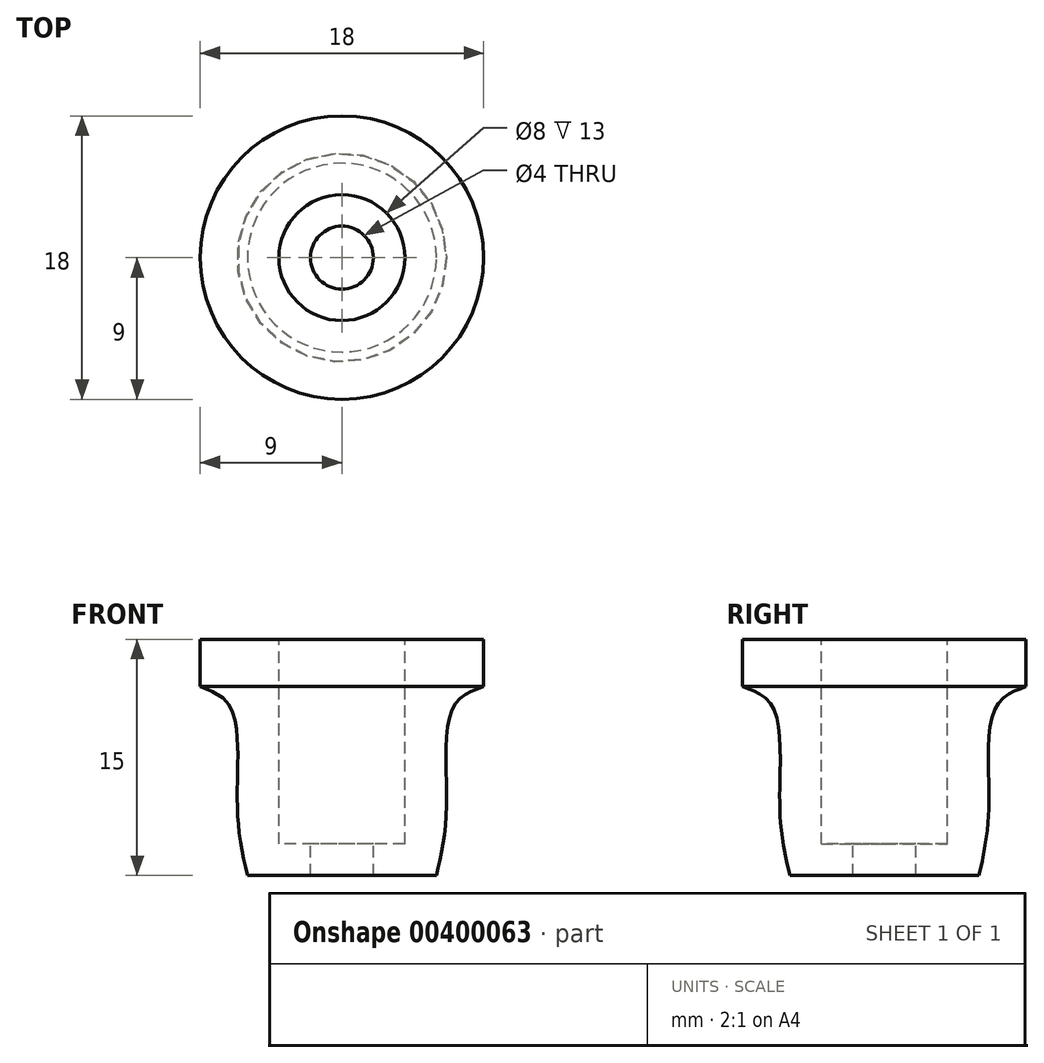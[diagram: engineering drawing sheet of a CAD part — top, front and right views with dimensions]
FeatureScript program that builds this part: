
annotation { "Feature Type Name" : "Feature", "Feature Type Description" : "" }
export const myFeature = defineFeature(function(context is Context, id is Id, definition is map)
    precondition{}
    {
        {
            var Q0;
            Q0=qCreatedBy(makeId("Front.planeOp"),FACE);
            var sketch = newSketch(context, id + "F0", { "sketchPlane" : qUnion([Q0])});
            skLineSegment(sketch, "E0", {"start": v(-9, 0) * mm, "end": v(-9, -3) * mm});
            skLineSegment(sketch, "E1", {"start": v(-6, -15) * mm, "end": v(-2, -15) * mm});
            skLineSegment(sketch, "E2", {"start": v(-2, -15) * mm, "end": v(-2, -13) * mm});
            skLineSegment(sketch, "E3", {"start": v(-9, 0) * mm, "end": v(-4, 0) * mm});
            skLineSegment(sketch, "E4", {"start": v(-4, 0) * mm, "end": v(-4, -13) * mm});
            skLineSegment(sketch, "E5", {"start": v(-4, -13) * mm, "end": v(-2, -13) * mm});
            skLineSegment(sketch, "E6", {"start": v(0, 0) * mm, "end": v(0, -16.45) * mm, "construction": true});
            skFitSpline(sketch, "E7", {"points": [v(-6, -15) * mm, v(-6.64, -10.66) * mm, v(-7.03, -4.39) * mm, v(-9, -3) * mm], "startDerivative": vector(-2.64, 11.32) * mm, "endDerivative": vector(-9.28, 3.3) * mm});
            skSolve(sketch);
        }
        {
            var Q0;
            Q0 = qSketchRegion(id + "F0", true);
            var Q1;
            Q1=sQuery(id+"F0.wireOp",EDGE,"E6");
            revolve(context, id + "F1", {"entities" : qUnion([Q0]), "axis" : qUnion([Q1]), "revolveType" : RevolveType.FULL});
        }
    });
